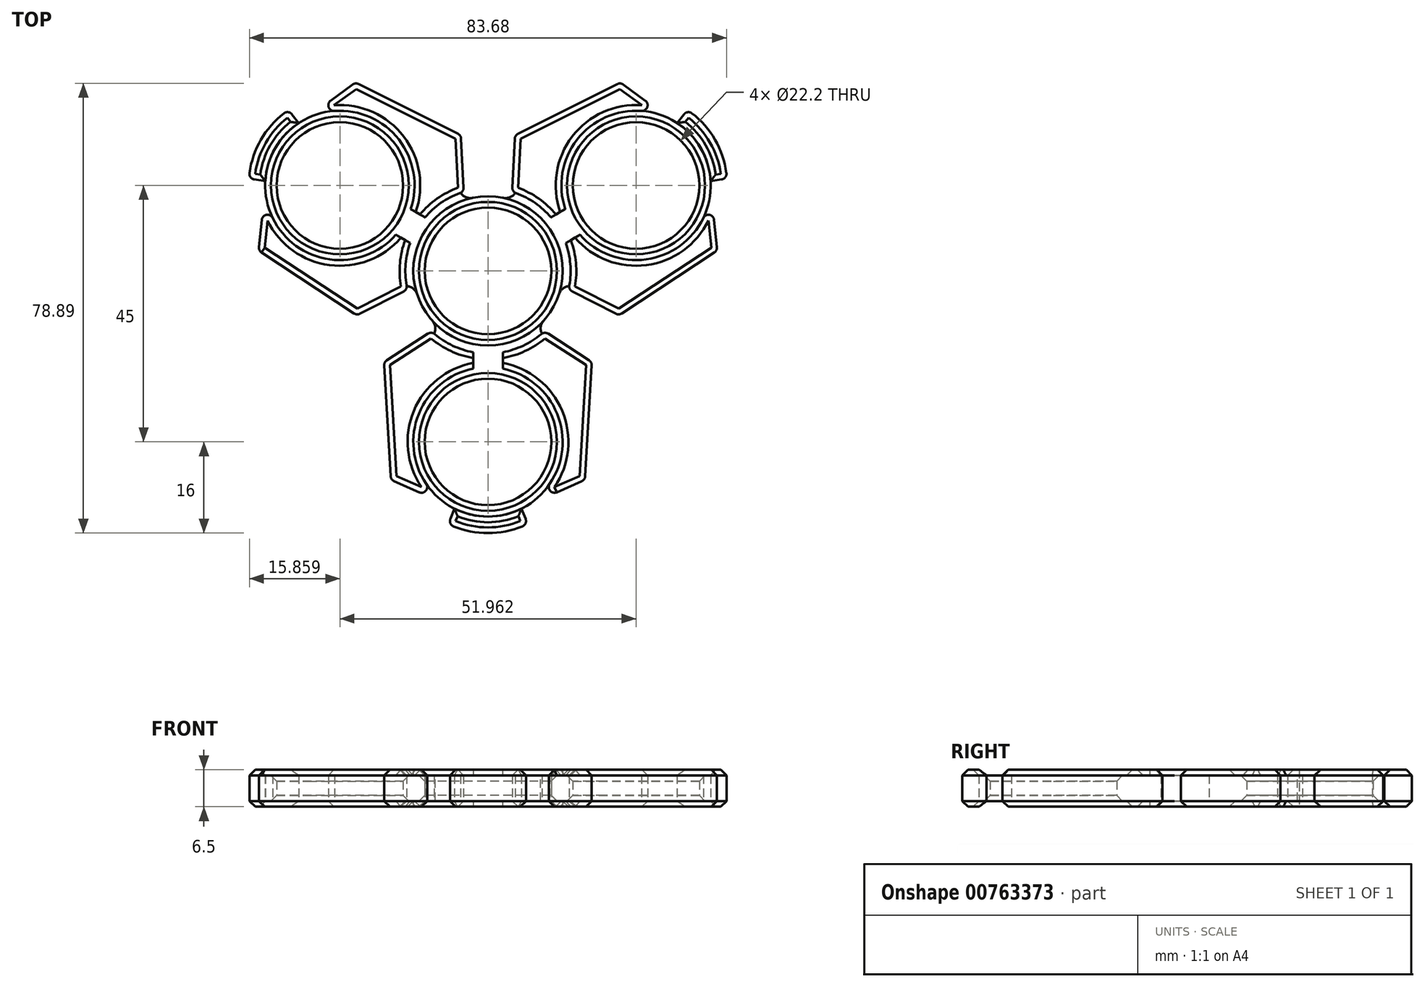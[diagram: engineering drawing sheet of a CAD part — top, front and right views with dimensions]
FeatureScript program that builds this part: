
annotation { "Feature Type Name" : "Feature", "Feature Type Description" : "" }
export const myFeature = defineFeature(function(context is Context, id is Id, definition is map)
    precondition{}
    {
        {
            var Q0;
            Q0=qCreatedBy(makeId("Top.planeOp"),FACE);
            var sketch = newSketch(context, id + "F0", { "sketchPlane" : qUnion([Q0])});
            skCircle(sketch, "E0", {"center": v(0, 0) * mm, "radius": 11.1 * mm});
            skCircle(sketch, "E1.0", {"center": v(0, 0) * mm, "radius": 13.1 * mm});
            skSolve(sketch);
        }
        {
            var Q0;
            Q0 = qSketchRegion(id + "F0", true);
            extrude(context, id + "F1", {"entities" : qUnion([Q0]), "depth" : 6.5 * mm, "offsetDistance" : 25 * mm});
        }
        {
            var Q0;
            Q0=qCreatedBy(makeId("Top.planeOp"),FACE);
            var sketch = newSketch(context, id + "F2", { "sketchPlane" : qUnion([Q0])});
            skCircle(sketch, "E2.cCircle", {"center": v(0, 0) * mm, "radius": 30 * mm, "construction": true});
            skLineSegment(sketch, "E2.0", {"start": v(0, -30) * mm, "end": v(-21.21, -21.21) * mm});
            skLineSegment(sketch, "E2.1", {"start": v(-21.21, -21.21) * mm, "end": v(-30, 0) * mm});
            skLineSegment(sketch, "E2.2", {"start": v(-30, 0) * mm, "end": v(-21.21, 21.21) * mm});
            skLineSegment(sketch, "E2.3", {"start": v(-21.21, 21.21) * mm, "end": v(0, 30) * mm});
            skLineSegment(sketch, "E2.4", {"start": v(0, 30) * mm, "end": v(21.21, 21.21) * mm});
            skLineSegment(sketch, "E2.5", {"start": v(21.21, 21.21) * mm, "end": v(30, 0) * mm});
            skLineSegment(sketch, "E2.6", {"start": v(30, 0) * mm, "end": v(21.21, -21.21) * mm});
            skLineSegment(sketch, "E2.7", {"start": v(21.21, -21.21) * mm, "end": v(0, -30) * mm});
            skCircle(sketch, "E3", {"center": v(0, -30) * mm, "radius": 11.1 * mm});
            skCircle(sketch, "E4.0", {"center": v(0, -30) * mm, "radius": 13.1 * mm});
            skLineSegment(sketch, "E5", {"start": v(0, -30) * mm, "end": v(0, -43.1) * mm});
            skLineSegment(sketch, "E6", {"start": v(0, -43.1) * mm, "end": v(18.52, -43.1) * mm});
            skLineSegment(sketch, "E7", {"start": v(25.6, -10.6) * mm, "end": v(31.04, -12.86) * mm});
            skLineSegment(sketch, "E8", {"start": v(31.04, -12.86) * mm, "end": v(18.52, -43.1) * mm});
            skPoint(sketch, "E9.start.orphan", {"position": v(22.4, -43.1) * mm});
            skLineSegment(sketch, "E10.MirrorCS", {"start": v(0, -43.1) * mm, "end": v(-18.52, -43.1) * mm});
            skLineSegment(sketch, "E11.MirrorCS", {"start": v(-31.04, -12.86) * mm, "end": v(-18.52, -43.1) * mm});
            skLineSegment(sketch, "E12.MirrorCS", {"start": v(-25.6, -10.6) * mm, "end": v(-31.04, -12.86) * mm});
            skLineSegment(sketch, "E13", {"start": v(25.6, -10.6) * mm, "end": v(12.1, -5.01) * mm});
            skLineSegment(sketch, "E14", {"start": v(21.21, -8.79) * mm, "end": v(16.05, -43.1) * mm});
            skLineSegment(sketch, "E15.MirrorCS", {"start": v(-21.21, -8.79) * mm, "end": v(-16.05, -43.1) * mm});
            skLineSegment(sketch, "E16.MirrorCS", {"start": v(-25.6, -10.6) * mm, "end": v(-12.1, -5.01) * mm});
            skCircle(sketch, "E17", {"center": v(0, 0) * mm, "radius": 13.1 * mm});
            skLineSegment(sketch, "E18", {"start": v(21.21, -21.21) * mm, "end": v(25.6, -10.6) * mm});
            skLineSegment(sketch, "E19", {"start": v(23.4, -15.9) * mm, "end": v(29.31, -18.35) * mm});
            skLineSegment(sketch, "E20", {"start": v(23.4, -15.9) * mm, "end": v(8.68, -9.8) * mm});
            skLineSegment(sketch, "E21.MirrorCS", {"start": v(-23.4, -15.9) * mm, "end": v(-8.68, -9.8) * mm});
            skLineSegment(sketch, "E22", {"start": v(8.68, -9.8) * mm, "end": v(19.96, -17.13) * mm});
            skPoint(sketch, "E22.endSnap0", {"position": v(26.36, -17.13) * mm});
            skLineSegment(sketch, "E23.MirrorCS", {"start": v(-8.68, -9.8) * mm, "end": v(-19.96, -17.13) * mm});
            skLineSegment(sketch, "E24", {"start": v(18.52, -43.1) * mm, "end": v(13.34, -55.6) * mm});
            skLineSegment(sketch, "E25", {"start": v(6.96, -41.1) * mm, "end": v(17.53, -45.47) * mm});
            skLineSegment(sketch, "E26.MirrorCS", {"start": v(-6.96, -41.1) * mm, "end": v(-17.53, -45.47) * mm});
            skLineSegment(sketch, "E27.MirrorCS", {"start": v(-18.52, -43.1) * mm, "end": v(-13.34, -55.6) * mm});
            skLineSegment(sketch, "E28.MirrorCS", {"start": v(-23.4, -15.9) * mm, "end": v(-29.31, -18.35) * mm});
            skLineSegment(sketch, "E29", {"start": v(16.05, -43.1) * mm, "end": v(14.56, -52.99) * mm});
            skLineSegment(sketch, "E30.MirrorCS", {"start": v(-16.05, -43.1) * mm, "end": v(-14.56, -52.99) * mm});
            skLineSegment(sketch, "E31", {"start": v(6.96, -41.1) * mm, "end": v(17.02, -36.64) * mm});
            skLineSegment(sketch, "E32.MirrorCS", {"start": v(-6.96, -41.1) * mm, "end": v(-17.02, -36.64) * mm});
            skLineSegment(sketch, "E33", {"start": v(0, -16.9) * mm, "end": v(0, -13.1) * mm});
            skLineSegment(sketch, "E34", {"start": v(2.6, -17.16) * mm, "end": v(2.6, -12.84) * mm});
            skLineSegment(sketch, "E35.MirrorCS", {"start": v(-2.6, -17.16) * mm, "end": v(-2.6, -12.84) * mm});
            skCircle(sketch, "E36", {"center": v(0, 0) * mm, "radius": 14.5 * mm});
            skLineSegment(sketch, "E37", {"start": v(8.68, -9.8) * mm, "end": v(8.68, 0) * mm});
            skLineSegment(sketch, "E38", {"start": v(8.68, 0) * mm, "end": v(0, 0) * mm});
            skLineSegment(sketch, "E39", {"start": v(17.02, -36.64) * mm, "end": v(18.23, -16) * mm});
            skPoint(sketch, "E40.orphan", {"position": v(17.02, -15.22) * mm});
            skPoint(sketch, "E41.orphan", {"position": v(-17.02, -15.22) * mm});
            skPoint(sketch, "E42.MirrorCS.start.orphan", {"position": v(-17.02, -36.64) * mm});
            skLineSegment(sketch, "E43.MirrorCS", {"start": v(-17.02, -36.64) * mm, "end": v(-18.23, -16) * mm});
            skCircle(sketch, "E44", {"center": v(0, -30) * mm, "radius": 16 * mm});
            skLineSegment(sketch, "E45", {"start": v(2.96, -42.76) * mm, "end": v(4.06, -45.48) * mm});
            skLineSegment(sketch, "E46.MirrorCS", {"start": v(-2.96, -42.76) * mm, "end": v(-4.06, -45.48) * mm});
            skLineSegment(sketch, "E47", {"start": v(-5.86, -41.72) * mm, "end": v(-6.96, -44.4) * mm});
            skLineSegment(sketch, "E48.MirrorCS", {"start": v(5.86, -41.72) * mm, "end": v(6.96, -44.4) * mm});
            skSolve(sketch);
        }
        {
            var Q0;
            {var subQ0=sQuery(id+"F2.wireOp",EDGE,"E4.0");var subQ1=sQuery(id+"F2.wireOp",EDGE,"E2.0");var subQ2=makeQuery(id+"F2.imprint","INTERSECT",VERTEX,{"derivedFrom":[subQ1,subQ0]});Q0=makeQuery(id+"F2.imprint","IMPRINT",FACE,{"disambiguationData":[TD([[makeQuery(id+"F2.imprint","IMPRINT",EDGE,{"disambiguationData":[TD([[subQ2,-1.0]])],"derivedFrom":subQ1}),-1.0]])]});}
            var Q1;
            {var subQ3=sQuery(id+"F2.wireOp",EDGE,"E2.0");var subQ5=sQuery(id+"F2.wireOp",EDGE,"E4.0");var subQ6=makeQuery(id+"F2.imprint","INTERSECT",VERTEX,{"derivedFrom":[subQ3,subQ5]});Q1=makeQuery(id+"F2.imprint","IMPRINT",FACE,{"disambiguationData":[TD([[makeQuery(id+"F2.imprint","IMPRINT",EDGE,{"disambiguationData":[TD([[subQ6,-1.0]])],"derivedFrom":subQ3}),1.0]])]});}
            var Q2;
            {var subQ5=sQuery(id+"F2.wireOp",EDGE,"E31");Q2=makeQuery(id+"F2.imprint","IMPRINT",FACE,{"disambiguationData":[TD([[makeQuery(id+"F2.imprint","IMPRINT",EDGE,{"derivedFrom":subQ5}),1.0]])]});}
            var Q3;
            {var subQ0=sQuery(id+"F2.wireOp",EDGE,"E39");var subQ8=sQuery(id+"F2.wireOp",EDGE,"E2.7");var subQ11=makeQuery(id+"F2.imprint","INTERSECT",VERTEX,{"derivedFrom":[subQ8,subQ0]});Q3=makeQuery(id+"F2.imprint","IMPRINT",FACE,{"disambiguationData":[TD([[makeQuery(id+"F2.imprint","IMPRINT",EDGE,{"disambiguationData":[TD([[subQ11,-1.0]])],"derivedFrom":subQ8}),-1.0]])]});}
            var Q4;
            {var subQ7=sQuery(id+"F2.wireOp",EDGE,"E44");var subQ9=sQuery(id+"F2.wireOp",EDGE,"E2.0");var subQ10=makeQuery(id+"F2.imprint","INTERSECT",VERTEX,{"derivedFrom":[subQ9,subQ7]});Q4=makeQuery(id+"F2.imprint","IMPRINT",FACE,{"disambiguationData":[TD([[makeQuery(id+"F2.imprint","IMPRINT",EDGE,{"disambiguationData":[TD([[subQ10,-1.0]])],"derivedFrom":subQ9}),-1.0]])]});}
            var Q5;
            {var subQ0=sQuery(id+"F2.wireOp",EDGE,"E44");var subQ1=sQuery(id+"F2.wireOp",EDGE,"E2.0");var subQ2=makeQuery(id+"F2.imprint","INTERSECT",VERTEX,{"derivedFrom":[subQ1,subQ0]});Q5=makeQuery(id+"F2.imprint","IMPRINT",FACE,{"disambiguationData":[TD([[makeQuery(id+"F2.imprint","IMPRINT",EDGE,{"disambiguationData":[TD([[subQ2,-1.0]])],"derivedFrom":subQ1}),1.0]])]});}
            var Q6;
            {var subQ0=sQuery(id+"F2.wireOp",EDGE,"E45");var subQ1=sQuery(id+"F2.wireOp",EDGE,"E44");var subQ2=makeQuery(id+"F2.imprint","INTERSECT",VERTEX,{"derivedFrom":[subQ1,subQ0]});Q6=makeQuery(id+"F2.imprint","IMPRINT",FACE,{"disambiguationData":[TD([[makeQuery(id+"F2.imprint","IMPRINT",EDGE,{"disambiguationData":[TD([[subQ2,1.0]])],"derivedFrom":subQ1}),1.0]])]});}
            var Q7;
            {var subQ1=sQuery(id+"F2.wireOp",EDGE,"E4.0");var subQ3=sQuery(id+"F2.wireOp",EDGE,"E46.MirrorCS");var subQ4=makeQuery(id+"F2.imprint","INTERSECT",VERTEX,{"derivedFrom":[subQ1,subQ3]});Q7=makeQuery(id+"F2.imprint","IMPRINT",FACE,{"disambiguationData":[TD([[makeQuery(id+"F2.imprint","IMPRINT",EDGE,{"disambiguationData":[TD([[subQ4,-1.0]])],"derivedFrom":subQ3}),1.0]])]});}
            var Q8;
            {var subQ1=sQuery(id+"F2.wireOp",EDGE,"E4.0");var subQ3=sQuery(id+"F2.wireOp",EDGE,"E45");var subQ4=makeQuery(id+"F2.imprint","INTERSECT",VERTEX,{"derivedFrom":[subQ1,subQ3]});Q8=makeQuery(id+"F2.imprint","IMPRINT",FACE,{"disambiguationData":[TD([[makeQuery(id+"F2.imprint","IMPRINT",EDGE,{"disambiguationData":[TD([[subQ4,-1.0]])],"derivedFrom":subQ3}),-1.0]])]});}
            var Q9;
            {var subQ0=sQuery(id+"F2.wireOp",EDGE,"E44");var subQ1=sQuery(id+"F2.wireOp",EDGE,"E2.7");var subQ2=makeQuery(id+"F2.imprint","INTERSECT",VERTEX,{"derivedFrom":[subQ1,subQ0]});Q9=makeQuery(id+"F2.imprint","IMPRINT",FACE,{"disambiguationData":[TD([[makeQuery(id+"F2.imprint","IMPRINT",EDGE,{"disambiguationData":[TD([[subQ2,-1.0]])],"derivedFrom":subQ1}),-1.0]])]});}
            var Q10;
            {var subQ0=sQuery(id+"F2.wireOp",EDGE,"E46.MirrorCS");var subQ1=sQuery(id+"F2.wireOp",EDGE,"E10.MirrorCS");var subQ2=makeQuery(id+"F2.imprint","INTERSECT",VERTEX,{"derivedFrom":[subQ1,subQ0]});Q10=makeQuery(id+"F2.imprint","IMPRINT",FACE,{"disambiguationData":[TD([[makeQuery(id+"F2.imprint","IMPRINT",EDGE,{"disambiguationData":[TD([[subQ2,-1.0]])],"derivedFrom":subQ1}),1.0]])]});}
            var Q11;
            {var subQ0=sQuery(id+"F2.wireOp",EDGE,"E45");var subQ1=sQuery(id+"F2.wireOp",EDGE,"E6");var subQ2=makeQuery(id+"F2.imprint","INTERSECT",VERTEX,{"derivedFrom":[subQ1,subQ0]});Q11=makeQuery(id+"F2.imprint","IMPRINT",FACE,{"disambiguationData":[TD([[makeQuery(id+"F2.imprint","IMPRINT",EDGE,{"disambiguationData":[TD([[subQ2,-1.0]])],"derivedFrom":subQ1}),-1.0]])]});}
            var Q12;
            {var subQ0=sQuery(id+"F2.wireOp",EDGE,"E45");var subQ1=sQuery(id+"F2.wireOp",EDGE,"E4.0");var subQ2=makeQuery(id+"F2.imprint","INTERSECT",VERTEX,{"derivedFrom":[subQ1,subQ0]});Q12=makeQuery(id+"F2.imprint","IMPRINT",FACE,{"disambiguationData":[TD([[makeQuery(id+"F2.imprint","IMPRINT",EDGE,{"disambiguationData":[TD([[subQ2,-1.0]])],"derivedFrom":subQ1}),-1.0]])]});}
            var Q13;
            {var subQ0=sQuery(id+"F2.wireOp",EDGE,"E46.MirrorCS");var subQ1=sQuery(id+"F2.wireOp",EDGE,"E4.0");var subQ2=makeQuery(id+"F2.imprint","INTERSECT",VERTEX,{"derivedFrom":[subQ1,subQ0]});Q13=makeQuery(id+"F2.imprint","IMPRINT",FACE,{"disambiguationData":[TD([[makeQuery(id+"F2.imprint","IMPRINT",EDGE,{"disambiguationData":[TD([[subQ2,1.0]])],"derivedFrom":subQ1}),-1.0]])]});}
            extrude(context, id + "F3", {"entities" : qUnion([Q0, Q1, Q2, Q3, Q4, Q5, Q6, Q7, Q8, Q9, Q10, Q11, Q12, Q13]), "depth" : 6.5 * mm, "offsetDistance" : 25 * mm});
        }
        {
            var Q0;
            Q0=makeQuery(id+"F3.opExtrude","SWEPT_EDGE",EDGE,{"disambiguationData":[OSD([sQuery(id+"F2.wireOp",EDGE,"E26.MirrorCS"),sQuery(id+"F2.wireOp",EDGE,"E30.MirrorCS")])]});
            var Q1;
            Q1=makeQuery(id+"F3.opExtrude","SWEPT_EDGE",EDGE,{"disambiguationData":[OSD([sQuery(id+"F2.wireOp",EDGE,"E25"),sQuery(id+"F2.wireOp",EDGE,"E29")])]});
            var Q2;
            Q2=makeQuery(id+"F3.opExtrude","SWEPT_EDGE",EDGE,{"disambiguationData":[OSD([sQuery(id+"F2.wireOp",EDGE,"E44"),sQuery(id+"F2.wireOp",EDGE,"E47")])]});
            var Q3;
            Q3=makeQuery(id+"F3.opExtrude","SWEPT_EDGE",EDGE,{"disambiguationData":[OSD([sQuery(id+"F2.wireOp",EDGE,"E44"),sQuery(id+"F2.wireOp",EDGE,"E48.MirrorCS")])]});
            fillet(context, id + "F4", {"entities" : qUnion([Q0, Q1, Q2, Q3]), "radius" : 1 * mm, "tangentPropagation" : true, "allowEdgeOverflow" : false});
        }
        {
            var Q0;
            Q0=makeQuery(id+"F3.opExtrude","SWEPT_EDGE",EDGE,{"disambiguationData":[OSD([sQuery(id+"F2.wireOp",EDGE,"E15.MirrorCS"),sQuery(id+"F2.wireOp",EDGE,"E23.MirrorCS")])]});
            var Q1;
            Q1=makeQuery(id+"F3.opExtrude","SWEPT_EDGE",EDGE,{"disambiguationData":[OSD([sQuery(id+"F2.wireOp",EDGE,"E14"),sQuery(id+"F2.wireOp",EDGE,"E22")])]});
            var Q2;
            Q2=makeQuery(id+"F3.opExtrude","SWEPT_EDGE",EDGE,{"disambiguationData":[OSD([sQuery(id+"F2.wireOp",EDGE,"E14"),sQuery(id+"F2.wireOp",EDGE,"E31"),sQuery(id+"F2.wireOp",EDGE,"E39")])]});
            var Q3;
            Q3=makeQuery(id+"F3.opExtrude","SWEPT_EDGE",EDGE,{"disambiguationData":[OSD([sQuery(id+"F2.wireOp",EDGE,"E15.MirrorCS"),sQuery(id+"F2.wireOp",EDGE,"E32.MirrorCS"),sQuery(id+"F2.wireOp",EDGE,"E43.MirrorCS")])]});
            fillet(context, id + "F5", {"entities" : qUnion([Q0, Q1, Q2, Q3]), "radius" : 1 * mm, "allowEdgeOverflow" : false});
        }
        {
            var Q0;
            Q0=makeQuery(id+"F1.opExtrude","CAP_EDGE",EDGE,{"disambiguationData":[OSD([sQuery(id+"F0.wireOp",EDGE,"E0")])],"isStart":false});
            var Q1;
            Q1=makeQuery(id+"F1.opExtrude","CAP_EDGE",EDGE,{"disambiguationData":[OSD([sQuery(id+"F0.wireOp",EDGE,"E0")])],"isStart":true});
            var Q2;
            {var subQ0=sQuery(id+"F2.wireOp",EDGE,"E4.0");var subQ1=makeQuery(id+"F2.imprint","INTERSECT",VERTEX,{"derivedFrom":[sQuery(id+"F2.wireOp",EDGE,"E2.7"),subQ0]});Q2=makeQuery(id+"F3.opExtrude","CAP_EDGE",EDGE,{"disambiguationData":[OSD([subQ0]),TDD([makeQuery(id+"F2.imprint","IMPRINT",EDGE,{"disambiguationData":[TD([[makeQuery(id+"F2.imprint","INTERSECT",VERTEX,{"derivedFrom":[subQ0,sQuery(id+"F2.wireOp",EDGE,"E34")]}),1.0]])],"derivedFrom":subQ0}),makeQuery(id+"F2.imprint","IMPRINT",EDGE,{"disambiguationData":[TD([[subQ1,1.0]])],"derivedFrom":subQ0})])],"isStart":false});}
            var Q3;
            {var subQ0=sQuery(id+"F2.wireOp",EDGE,"E4.0");var subQ1=makeQuery(id+"F2.imprint","INTERSECT",VERTEX,{"derivedFrom":[sQuery(id+"F2.wireOp",EDGE,"E2.0"),subQ0]});Q3=makeQuery(id+"F3.opExtrude","CAP_EDGE",EDGE,{"disambiguationData":[OSD([subQ0]),TDD([makeQuery(id+"F2.imprint","IMPRINT",EDGE,{"disambiguationData":[TD([[makeQuery(id+"F2.imprint","INTERSECT",VERTEX,{"derivedFrom":[subQ0,sQuery(id+"F2.wireOp",EDGE,"E35.MirrorCS")]}),-1.0]])],"derivedFrom":subQ0}),makeQuery(id+"F2.imprint","IMPRINT",EDGE,{"disambiguationData":[TD([[subQ1,-1.0]])],"derivedFrom":subQ0})])],"isStart":false});}
            var Q4;
            {var subQ0=sQuery(id+"F2.wireOp",EDGE,"E4.0");var subQ1=makeQuery(id+"F2.imprint","INTERSECT",VERTEX,{"derivedFrom":[sQuery(id+"F2.wireOp",EDGE,"E2.0"),subQ0]});Q4=makeQuery(id+"F3.opExtrude","CAP_EDGE",EDGE,{"disambiguationData":[OSD([subQ0]),TDD([makeQuery(id+"F2.imprint","IMPRINT",EDGE,{"disambiguationData":[TD([[makeQuery(id+"F2.imprint","INTERSECT",VERTEX,{"derivedFrom":[subQ0,sQuery(id+"F2.wireOp",EDGE,"E35.MirrorCS")]}),-1.0]])],"derivedFrom":subQ0}),makeQuery(id+"F2.imprint","IMPRINT",EDGE,{"disambiguationData":[TD([[subQ1,-1.0]])],"derivedFrom":subQ0})])],"isStart":true});}
            var Q5;
            {var subQ0=sQuery(id+"F2.wireOp",EDGE,"E4.0");var subQ1=makeQuery(id+"F2.imprint","INTERSECT",VERTEX,{"derivedFrom":[sQuery(id+"F2.wireOp",EDGE,"E2.7"),subQ0]});Q5=makeQuery(id+"F3.opExtrude","CAP_EDGE",EDGE,{"disambiguationData":[OSD([subQ0]),TDD([makeQuery(id+"F2.imprint","IMPRINT",EDGE,{"disambiguationData":[TD([[makeQuery(id+"F2.imprint","INTERSECT",VERTEX,{"derivedFrom":[subQ0,sQuery(id+"F2.wireOp",EDGE,"E34")]}),1.0]])],"derivedFrom":subQ0}),makeQuery(id+"F2.imprint","IMPRINT",EDGE,{"disambiguationData":[TD([[subQ1,1.0]])],"derivedFrom":subQ0})])],"isStart":true});}
            var Q6;
            Q6=makeQuery(id+"F3.opExtrude","CAP_EDGE",EDGE,{"disambiguationData":[OSD([sQuery(id+"F2.wireOp",EDGE,"E44")])],"isStart":true});
            var Q7;
            Q7=makeQuery(id+"F3.opExtrude","CAP_EDGE",EDGE,{"disambiguationData":[OSD([sQuery(id+"F2.wireOp",EDGE,"E44")])],"isStart":false});
            var Q8;
            {var subQ0=sQuery(id+"F2.wireOp",EDGE,"E4.0");var subQ1=makeQuery(id+"F2.imprint","INTERSECT",VERTEX,{"derivedFrom":[subQ0,sQuery(id+"F2.wireOp",EDGE,"E45")]});var subQ3=makeQuery(id+"F2.imprint","INTERSECT",VERTEX,{"derivedFrom":[subQ0,sQuery(id+"F2.wireOp",EDGE,"E46.MirrorCS")]});Q8=makeQuery(id+"F3.opExtrude","CAP_EDGE",EDGE,{"disambiguationData":[OSD([subQ0]),TDD([makeQuery(id+"F2.imprint","IMPRINT",EDGE,{"disambiguationData":[TD([[subQ3,1.0]])],"derivedFrom":subQ0}),makeQuery(id+"F2.imprint","IMPRINT",EDGE,{"disambiguationData":[TD([[subQ3,-1.0]])],"derivedFrom":subQ0}),makeQuery(id+"F2.imprint","IMPRINT",EDGE,{"disambiguationData":[TD([[subQ1,1.0]])],"derivedFrom":subQ0}),makeQuery(id+"F2.imprint","IMPRINT",EDGE,{"disambiguationData":[TD([[subQ1,-1.0]])],"derivedFrom":subQ0})])],"isStart":false});}
            var Q9;
            {var subQ0=sQuery(id+"F2.wireOp",EDGE,"E4.0");var subQ1=makeQuery(id+"F2.imprint","INTERSECT",VERTEX,{"derivedFrom":[subQ0,sQuery(id+"F2.wireOp",EDGE,"E45")]});var subQ3=makeQuery(id+"F2.imprint","INTERSECT",VERTEX,{"derivedFrom":[subQ0,sQuery(id+"F2.wireOp",EDGE,"E46.MirrorCS")]});Q9=makeQuery(id+"F3.opExtrude","CAP_EDGE",EDGE,{"disambiguationData":[OSD([subQ0]),TDD([makeQuery(id+"F2.imprint","IMPRINT",EDGE,{"disambiguationData":[TD([[subQ3,1.0]])],"derivedFrom":subQ0}),makeQuery(id+"F2.imprint","IMPRINT",EDGE,{"disambiguationData":[TD([[subQ3,-1.0]])],"derivedFrom":subQ0}),makeQuery(id+"F2.imprint","IMPRINT",EDGE,{"disambiguationData":[TD([[subQ1,1.0]])],"derivedFrom":subQ0}),makeQuery(id+"F2.imprint","IMPRINT",EDGE,{"disambiguationData":[TD([[subQ1,-1.0]])],"derivedFrom":subQ0})])],"isStart":true});}
            chamfer(context, id + "F6", {"entities" : qUnion([Q0, Q1, Q2, Q3, Q4, Q5, Q6, Q7, Q8, Q9]), "width" : 1 * mm, "tangentPropagation" : true});
        }
        {
            var Q0;
            Q0=makeQuery(id+"F3.opExtrude","SWEPT_BODY",BODY,{"disambiguationData":[OSD([sQuery(id+"F2.wireOp",EDGE,"E2.0"),sQuery(id+"F2.wireOp",EDGE,"E2.1"),sQuery(id+"F2.wireOp",EDGE,"E2.6"),sQuery(id+"F2.wireOp",EDGE,"E2.7"),sQuery(id+"F2.wireOp",EDGE,"E3"),sQuery(id+"F2.wireOp",EDGE,"E4.0"),sQuery(id+"F2.wireOp",EDGE,"E6"),sQuery(id+"F2.wireOp",EDGE,"E7"),sQuery(id+"F2.wireOp",EDGE,"E8"),sQuery(id+"F2.wireOp",EDGE,"E10.MirrorCS"),sQuery(id+"F2.wireOp",EDGE,"E11.MirrorCS"),sQuery(id+"F2.wireOp",EDGE,"E12.MirrorCS")])]});
            var Q1;
            Q1=makeQuery(id+"F3.opExtrude","SWEPT_BODY",BODY,{"disambiguationData":[OSD([sQuery(id+"F2.wireOp",EDGE,"E4.0"),sQuery(id+"F2.wireOp",EDGE,"E23.MirrorCS"),sQuery(id+"F2.wireOp",EDGE,"E32.MirrorCS"),sQuery(id+"F2.wireOp",EDGE,"E35.MirrorCS"),sQuery(id+"F2.wireOp",EDGE,"E36"),sQuery(id+"F2.wireOp",EDGE,"E43.MirrorCS")])]});
            var Q2;
            Q2=makeQuery(id+"F3.opExtrude","SWEPT_BODY",BODY,{"disambiguationData":[OSD([sQuery(id+"F2.wireOp",EDGE,"E4.0"),sQuery(id+"F2.wireOp",EDGE,"E22"),sQuery(id+"F2.wireOp",EDGE,"E31"),sQuery(id+"F2.wireOp",EDGE,"E34"),sQuery(id+"F2.wireOp",EDGE,"E36"),sQuery(id+"F2.wireOp",EDGE,"E39")])]});
            var Q3;
            {var subQ0=sQuery(id+"F0.wireOp",EDGE,"E0");Q3=makeQuery(id+"F6.opChamfer","BLEND_EDGE",EDGE,{"blendedFrom":[makeQuery(id+"F1.opExtrude","CAP_EDGE",EDGE,{"disambiguationData":[OSD([subQ0])],"isStart":false}),makeQuery(id+"F1.opExtrude","SWEPT_FACE",FACE,{"disambiguationData":[OSD([subQ0])]})],"blendedInto":[makeQuery(id+"F1.opExtrude","SWEPT_FACE",FACE,{"disambiguationData":[OSD([subQ0])]})]});}
            circularPattern(context, id + "F7", {"entities" : qUnion([Q0, Q1, Q2]), "axis" : qUnion([Q3]), "angle" : 360 * degree, "instanceCount" : 3, "equalSpace" : true});
        }
        {
            var Q0;
            Q0=qCreatedBy(makeId("Top.planeOp"),FACE);
            cPlane(context, id + "F8", {"entities" : qUnion([Q0]), "cplaneType" : CPlaneType.OFFSET, "offset" : 1 * mm, "width" : 150 * mm, "height" : 150 * mm});
        }
        {
            var Q0;
            Q0=qCreatedBy(id+"F8.planeOp",FACE);
            var sketch = newSketch(context, id + "F9", { "sketchPlane" : qUnion([Q0])});
            skCircle(sketch, "E49", {"center": v(0, 0) * mm, "radius": 30 * mm});
            skCircle(sketch, "E50", {"center": v(0, -30) * mm, "radius": 11.1 * mm});
            skCircle(sketch, "E51.0", {"center": v(0, -30) * mm, "radius": 13.1 * mm});
            skLineSegment(sketch, "E52", {"start": v(0, 0) * mm, "end": v(7.8, 0) * mm});
            skLineSegment(sketch, "E53", {"start": v(7.8, 0) * mm, "end": v(7.8, -9.8) * mm});
            skLineSegment(sketch, "E54", {"start": v(7.8, -9.8) * mm, "end": v(15.37, -15.3) * mm});
            skLineSegment(sketch, "E55", {"start": v(0, 0) * mm, "end": v(0, -7.45) * mm});
            skLineSegment(sketch, "E56.MirrorCS", {"start": v(-7.8, -9.8) * mm, "end": v(-15.37, -15.3) * mm});
            skLineSegment(sketch, "E57", {"start": v(-15.37, -15.3) * mm, "end": v(-8.14, -19.74) * mm});
            skLineSegment(sketch, "E58.MirrorCS", {"start": v(15.37, -15.3) * mm, "end": v(8.14, -19.74) * mm});
            skCircle(sketch, "E59", {"center": v(0, 0) * mm, "radius": 12.53 * mm});
            skSolve(sketch);
        }
        {
            var Q0;
            {var subQ0=sQuery(id+"F9.wireOp",EDGE,"E51.0");var subQ1=sQuery(id+"F9.wireOp",EDGE,"E49");var subQ2=makeQuery(id+"F9.imprint","INTERSECT",VERTEX,{"disambiguationData":[OD(0.0)],"derivedFrom":[subQ1,subQ0]});Q0=makeQuery(id+"F9.imprint","IMPRINT",FACE,{"disambiguationData":[TD([[makeQuery(id+"F9.imprint","IMPRINT",EDGE,{"disambiguationData":[TD([[subQ2,-1.0]])],"derivedFrom":subQ1}),-1.0]])]});}
            var Q1;
            {var subQ0=sQuery(id+"F9.wireOp",EDGE,"E51.0");var subQ1=sQuery(id+"F9.wireOp",EDGE,"E49");var subQ2=makeQuery(id+"F9.imprint","INTERSECT",VERTEX,{"disambiguationData":[OD(0.0)],"derivedFrom":[subQ1,subQ0]});Q1=makeQuery(id+"F9.imprint","IMPRINT",FACE,{"disambiguationData":[TD([[makeQuery(id+"F9.imprint","IMPRINT",EDGE,{"disambiguationData":[TD([[subQ2,-1.0]])],"derivedFrom":subQ1}),1.0]])]});}
            var Q2;
            {var subQ1=sQuery(id+"F9.wireOp",EDGE,"E54");Q2=makeQuery(id+"F9.imprint","IMPRINT",FACE,{"disambiguationData":[TD([[makeQuery(id+"F9.imprint","IMPRINT",EDGE,{"derivedFrom":subQ1}),-1.0]])]});}
            extrude(context, id + "F10", {"entities" : qUnion([Q0, Q1, Q2]), "depth" : 4.5 * mm, "offsetDistance" : 25 * mm});
        }
        {
            var Q0;
            Q0=makeQuery(id+"F10.opExtrude","CAP_EDGE",EDGE,{"disambiguationData":[OSD([sQuery(id+"F9.wireOp",EDGE,"E50")])],"isStart":false});
            var Q1;
            Q1=makeQuery(id+"F10.opExtrude","CAP_EDGE",EDGE,{"disambiguationData":[OSD([sQuery(id+"F9.wireOp",EDGE,"E50")])],"isStart":true});
            chamfer(context, id + "F11", {"entities" : qUnion([Q0, Q1]), "width" : 1 * mm, "tangentPropagation" : true});
        }
        {
            var Q0;
            Q0=makeQuery(id+"F10.opExtrude","SWEPT_BODY",BODY,{"disambiguationData":[OSD([sQuery(id+"F9.wireOp",EDGE,"E50"),sQuery(id+"F9.wireOp",EDGE,"E51.0")])]});
            var Q1;
            Q1=makeQuery(id+"F1.opExtrude","SWEPT_FACE",FACE,{"disambiguationData":[OSD([sQuery(id+"F0.wireOp",EDGE,"E0")])]});
            circularPattern(context, id + "F12", {"entities" : qUnion([Q0]), "axis" : qUnion([Q1]), "angle" : 360 * degree, "instanceCount" : 3, "equalSpace" : true});
        }
        {
            var Q0;
            Q0=makeQuery(id+"F1.opExtrude","SWEPT_BODY",BODY,{"disambiguationData":[OSD([sQuery(id+"F0.wireOp",EDGE,"E0"),sQuery(id+"F0.wireOp",EDGE,"E1.0")])]});
            var Q1;
            Q1=makeQuery(id+"F3.opExtrude","SWEPT_BODY",BODY,{"disambiguationData":[OSD([sQuery(id+"F2.wireOp",EDGE,"E4.0"),sQuery(id+"F2.wireOp",EDGE,"E14"),sQuery(id+"F2.wireOp",EDGE,"E22"),sQuery(id+"F2.wireOp",EDGE,"E31"),sQuery(id+"F2.wireOp",EDGE,"E34"),sQuery(id+"F2.wireOp",EDGE,"E36")])]});
            var Q2;
            Q2=makeQuery(id+"F3.opExtrude","SWEPT_BODY",BODY,{"disambiguationData":[OSD([sQuery(id+"F2.wireOp",EDGE,"E4.0"),sQuery(id+"F2.wireOp",EDGE,"E15.MirrorCS"),sQuery(id+"F2.wireOp",EDGE,"E23.MirrorCS"),sQuery(id+"F2.wireOp",EDGE,"E32.MirrorCS"),sQuery(id+"F2.wireOp",EDGE,"E35.MirrorCS"),sQuery(id+"F2.wireOp",EDGE,"E36")])]});
            var Q3;
            Q3=makeQuery(id+"F10.opExtrude","SWEPT_BODY",BODY,{"disambiguationData":[OSD([sQuery(id+"F9.wireOp",EDGE,"E50"),sQuery(id+"F9.wireOp",EDGE,"E51.0"),sQuery(id+"F9.wireOp",EDGE,"E54"),sQuery(id+"F9.wireOp",EDGE,"E56.MirrorCS"),sQuery(id+"F9.wireOp",EDGE,"E57"),sQuery(id+"F9.wireOp",EDGE,"E58.MirrorCS"),sQuery(id+"F9.wireOp",EDGE,"E59")])]});
            var Q4;
            Q4=makeQuery(id+"F12.opPattern","COPY",BODY,{"derivedFrom":makeQuery(id+"F10.opExtrude","SWEPT_BODY",BODY,{"disambiguationData":[OSD([sQuery(id+"F9.wireOp",EDGE,"E50"),sQuery(id+"F9.wireOp",EDGE,"E51.0"),sQuery(id+"F9.wireOp",EDGE,"E54"),sQuery(id+"F9.wireOp",EDGE,"E56.MirrorCS"),sQuery(id+"F9.wireOp",EDGE,"E57"),sQuery(id+"F9.wireOp",EDGE,"E58.MirrorCS"),sQuery(id+"F9.wireOp",EDGE,"E59")])]}),"instanceName":"1"});
            var Q5;
            Q5=makeQuery(id+"F7.opPattern","COPY",BODY,{"derivedFrom":makeQuery(id+"F3.opExtrude","SWEPT_BODY",BODY,{"disambiguationData":[OSD([sQuery(id+"F2.wireOp",EDGE,"E4.0"),sQuery(id+"F2.wireOp",EDGE,"E14"),sQuery(id+"F2.wireOp",EDGE,"E22"),sQuery(id+"F2.wireOp",EDGE,"E31"),sQuery(id+"F2.wireOp",EDGE,"E34"),sQuery(id+"F2.wireOp",EDGE,"E36")])]}),"instanceName":"1"});
            var Q6;
            Q6=makeQuery(id+"F7.opPattern","COPY",BODY,{"derivedFrom":makeQuery(id+"F3.opExtrude","SWEPT_BODY",BODY,{"disambiguationData":[OSD([sQuery(id+"F2.wireOp",EDGE,"E4.0"),sQuery(id+"F2.wireOp",EDGE,"E15.MirrorCS"),sQuery(id+"F2.wireOp",EDGE,"E23.MirrorCS"),sQuery(id+"F2.wireOp",EDGE,"E32.MirrorCS"),sQuery(id+"F2.wireOp",EDGE,"E35.MirrorCS"),sQuery(id+"F2.wireOp",EDGE,"E36")])]}),"instanceName":"1"});
            var Q7;
            Q7=makeQuery(id+"F7.opPattern","COPY",BODY,{"derivedFrom":makeQuery(id+"F3.opExtrude","SWEPT_BODY",BODY,{"disambiguationData":[OSD([sQuery(id+"F2.wireOp",EDGE,"E4.0"),sQuery(id+"F2.wireOp",EDGE,"E15.MirrorCS"),sQuery(id+"F2.wireOp",EDGE,"E23.MirrorCS"),sQuery(id+"F2.wireOp",EDGE,"E32.MirrorCS"),sQuery(id+"F2.wireOp",EDGE,"E35.MirrorCS"),sQuery(id+"F2.wireOp",EDGE,"E36")])]}),"instanceName":"2"});
            var Q8;
            Q8=makeQuery(id+"F12.opPattern","COPY",BODY,{"derivedFrom":makeQuery(id+"F10.opExtrude","SWEPT_BODY",BODY,{"disambiguationData":[OSD([sQuery(id+"F9.wireOp",EDGE,"E50"),sQuery(id+"F9.wireOp",EDGE,"E51.0"),sQuery(id+"F9.wireOp",EDGE,"E54"),sQuery(id+"F9.wireOp",EDGE,"E56.MirrorCS"),sQuery(id+"F9.wireOp",EDGE,"E57"),sQuery(id+"F9.wireOp",EDGE,"E58.MirrorCS"),sQuery(id+"F9.wireOp",EDGE,"E59")])]}),"instanceName":"2"});
            var Q9;
            Q9=makeQuery(id+"F7.opPattern","COPY",BODY,{"derivedFrom":makeQuery(id+"F3.opExtrude","SWEPT_BODY",BODY,{"disambiguationData":[OSD([sQuery(id+"F2.wireOp",EDGE,"E4.0"),sQuery(id+"F2.wireOp",EDGE,"E14"),sQuery(id+"F2.wireOp",EDGE,"E22"),sQuery(id+"F2.wireOp",EDGE,"E31"),sQuery(id+"F2.wireOp",EDGE,"E34"),sQuery(id+"F2.wireOp",EDGE,"E36")])]}),"instanceName":"2"});
            booleanBodies(context, id + "F13", {"operationType" : BooleanOperationType.UNION, "tools" : qUnion([Q0, Q1, Q2, Q3, Q4, Q5, Q6, Q7, Q8, Q9])});
        }
        {
            var Q0;
            Q0=makeQuery(id+"F13.opBoolean","INTERSECT",EDGE,{"derivedFrom":[makeQuery(id+"F1.opExtrude","SWEPT_FACE",FACE,{"disambiguationData":[OSD([sQuery(id+"F0.wireOp",EDGE,"E1.0")])]}),makeQuery(id+"F10.opExtrude","SWEPT_FACE",FACE,{"disambiguationData":[OSD([sQuery(id+"F9.wireOp",EDGE,"E56.MirrorCS")])]})]});
            var Q1;
            Q1=makeQuery(id+"F13.opBoolean","INTERSECT",EDGE,{"derivedFrom":[makeQuery(id+"F1.opExtrude","SWEPT_FACE",FACE,{"disambiguationData":[OSD([sQuery(id+"F0.wireOp",EDGE,"E1.0")])]}),makeQuery(id+"F10.opExtrude","SWEPT_FACE",FACE,{"disambiguationData":[OSD([sQuery(id+"F9.wireOp",EDGE,"E54")])]})]});
            var Q2;
            Q2=makeQuery(id+"F13.opBoolean","INTERSECT",EDGE,{"derivedFrom":[makeQuery(id+"F1.opExtrude","SWEPT_FACE",FACE,{"disambiguationData":[OSD([sQuery(id+"F0.wireOp",EDGE,"E1.0")])]}),makeQuery(id+"F12.opPattern","COPY",FACE,{"derivedFrom":makeQuery(id+"F10.opExtrude","SWEPT_FACE",FACE,{"disambiguationData":[OSD([sQuery(id+"F9.wireOp",EDGE,"E54")])]}),"instanceName":"2"})]});
            var Q3;
            Q3=makeQuery(id+"F13.opBoolean","INTERSECT",EDGE,{"derivedFrom":[makeQuery(id+"F1.opExtrude","SWEPT_FACE",FACE,{"disambiguationData":[OSD([sQuery(id+"F0.wireOp",EDGE,"E1.0")])]}),makeQuery(id+"F12.opPattern","COPY",FACE,{"derivedFrom":makeQuery(id+"F10.opExtrude","SWEPT_FACE",FACE,{"disambiguationData":[OSD([sQuery(id+"F9.wireOp",EDGE,"E56.MirrorCS")])]}),"instanceName":"1"})]});
            var Q4;
            Q4=makeQuery(id+"F13.opBoolean","INTERSECT",EDGE,{"derivedFrom":[makeQuery(id+"F1.opExtrude","SWEPT_FACE",FACE,{"disambiguationData":[OSD([sQuery(id+"F0.wireOp",EDGE,"E1.0")])]}),makeQuery(id+"F12.opPattern","COPY",FACE,{"derivedFrom":makeQuery(id+"F10.opExtrude","SWEPT_FACE",FACE,{"disambiguationData":[OSD([sQuery(id+"F9.wireOp",EDGE,"E56.MirrorCS")])]}),"instanceName":"2"})]});
            var Q5;
            Q5=makeQuery(id+"F13.opBoolean","INTERSECT",EDGE,{"derivedFrom":[makeQuery(id+"F1.opExtrude","SWEPT_FACE",FACE,{"disambiguationData":[OSD([sQuery(id+"F0.wireOp",EDGE,"E1.0")])]}),makeQuery(id+"F12.opPattern","COPY",FACE,{"derivedFrom":makeQuery(id+"F10.opExtrude","SWEPT_FACE",FACE,{"disambiguationData":[OSD([sQuery(id+"F9.wireOp",EDGE,"E54")])]}),"instanceName":"1"})]});
            fillet(context, id + "F14", {"entities" : qUnion([Q0, Q1, Q2, Q3, Q4, Q5]), "radius" : 2 * mm, "tangentPropagation" : true, "allowEdgeOverflow" : false});
        }
    });
